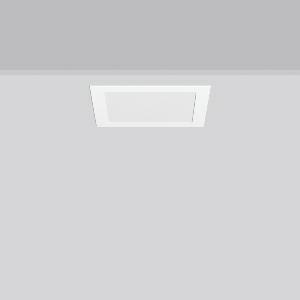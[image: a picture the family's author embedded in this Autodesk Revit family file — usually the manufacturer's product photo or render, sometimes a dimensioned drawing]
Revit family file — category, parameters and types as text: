
# Revit family: toledo_flat_square_e_901487_002_7142
name_source: partatom
category: Lighting Fixtures
units: mm (PartAtom-declared; Revit-internal decimal feet)

## family parameters
Cut with Voids When Loaded = No
Host = Face
Light Source = No
Part Type = Normal
Room Calculation Point = No
Round Connector Dimension = Use Diameter
Shared = No

## types (1)
- TOLEDO FLAT square E (1 x LED Modul 830, 1650 lm, 3000)
    Apparent Load = 17 VA
    CIE Flux Codes = 48 80 96 100 100
    Color Rendering = 80
    Color Temperature = 3000
    Default Elevation = 1800 mm
    Description = Series: TOLEDO FLAT square
Ultra thin recessed downlight. Housing: die-cast aluminium. Light guide and diffuser made of non-yellowing PMMA, opal matt. Ceiling installation with spring system. Mounting depth depends on ceiling strength. Suitable for through-wiring with separately available accessories. Surface mounted housing as accessory for all sizes. Retrofittable decorative cylinders made of chintz fabric as accessory, optional with satin finish plastic diffuser. Through-wiring box (5 pole) available as accessory. 
Colour: white
Length: 225 mm
Width: 225 mm
Height: 3 mm
Cut-out length: 208 mm
Cut-out width: 208 mm
Recess height: 29-56 mm
Luminaire: recess height: 31-51 mm
Lamp: LED
Socket: without socket
Colour temperature: 3000K
Colour rendering index (CRI): 80
System power: 17 W
Rated luminous flux: 1650 lm
Luminous efficiency: 97 lm/W
Control gear: Regulated power supply
Protection class: II
Type of protection: IP 54
    Height = 0 mm  [stored 0 ft]
    Lamp = 1 x LED Modul 830
    Lamp Light Flux = 1650 lm
    Lamp count = 1
    Length = 225 mm
    Lifetime = 50000 h
    Luminous efficacy = 97 lm/W
    Manufacturer = RZB
    ModVariant = No
    Model = 901487.002
    Mounting Place = Ceiling
    Mounting Type = Recessed
    Number of Poles = 1
    OnlyDefault = Yes
    Power Factor = 1
    Product Name = TOLEDO FLAT square E
    Product group = Recessed downlights
    ProductGroupID = 402
    Protection Class = Protection class II
    Protection Degree = IP 20
    RLX_Detail_Level = 1
    RLX_Emergency_Light_Flux = 0 lm
    RLX_Emergency_Type = 0
    RLX_Emergency_Type_DB = No
    RlxData = <blob elided: 58905 chars, md5=cd8308f0>
    Socket = socket
    Standby Power = 0 W
    System Light Flux = 1650 lm
    System Power = 17 W
    Type Comments = Product without accessories
    Type Image = 901487.002.jpg
    URL = http://relux.com
    VarID = ---
    Voltage = 230 V
    Voltage Range = 220-240 V
    Weight = 0.00 kg
    Width = 225 mm

note: [stored X ft] marks values corroborated as IEEE doubles in the binary element streams (Revit-internal decimal feet)

## geometry (parser evidence)
native form markers: Blend x4, Sweep x11
no freeform markers — native parametric forms only
